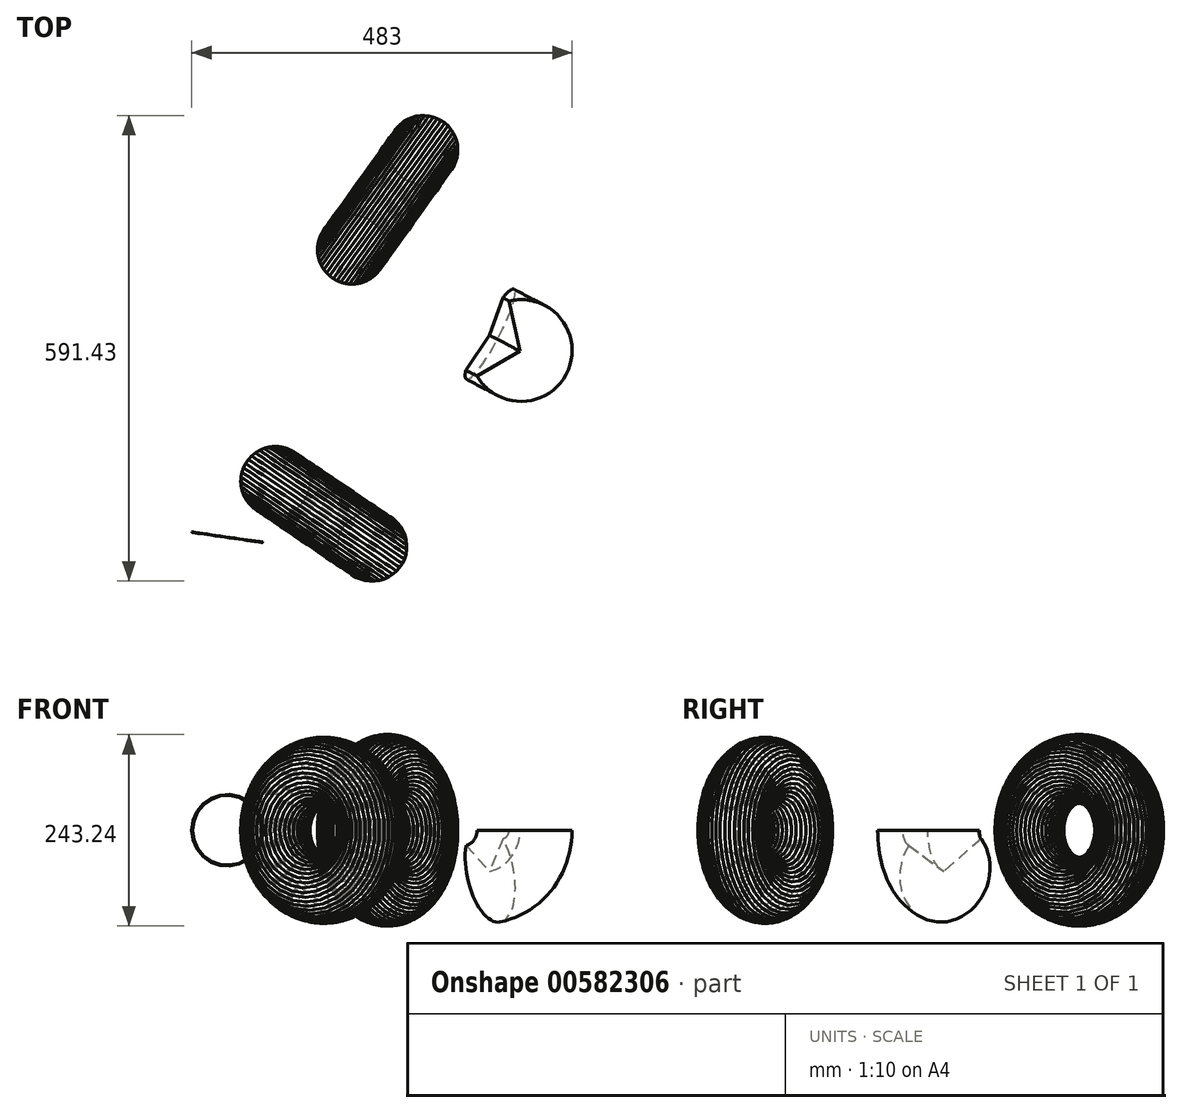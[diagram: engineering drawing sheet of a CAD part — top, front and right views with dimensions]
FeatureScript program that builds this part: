
annotation { "Feature Type Name" : "Feature", "Feature Type Description" : "" }
export const myFeature = defineFeature(function(context is Context, id is Id, definition is map)
    precondition{}
    {
        {
            var Q0;
            Q0=qCreatedBy(makeId("Top.planeOp"),FACE);
            var sketch = newSketch(context, id + "F0", { "sketchPlane" : qUnion([Q0])});
            skCircle(sketch, "E0.cCircle", {"center": v(-34.24, 57.95) * mm, "radius": 43.92 * mm, "construction": true});
            skLineSegment(sketch, "E0.0", {"start": v(1.92, 32.83) * mm, "end": v(-1.92, 28.04) * mm});
            skLineSegment(sketch, "E0.1", {"start": v(-1.92, 28.04) * mm, "end": v(-6.4, 23.84) * mm});
            skLineSegment(sketch, "E0.2", {"start": v(-6.4, 23.84) * mm, "end": v(-11.42, 20.3) * mm});
            skLineSegment(sketch, "E0.3", {"start": v(-11.42, 20.3) * mm, "end": v(-16.88, 17.48) * mm});
            skLineSegment(sketch, "E0.4", {"start": v(-16.88, 17.48) * mm, "end": v(-22.68, 15.46) * mm});
            skLineSegment(sketch, "E0.5", {"start": v(-22.68, 15.46) * mm, "end": v(-28.7, 14.27) * mm});
            skLineSegment(sketch, "E0.6", {"start": v(-28.7, 14.27) * mm, "end": v(-34.84, 13.92) * mm});
            skLineSegment(sketch, "E0.7", {"start": v(-34.84, 13.92) * mm, "end": v(-40.96, 14.44) * mm});
            skLineSegment(sketch, "E0.8", {"start": v(-40.96, 14.44) * mm, "end": v(-46.95, 15.8) * mm});
            skLineSegment(sketch, "E0.9", {"start": v(-46.95, 15.8) * mm, "end": v(-52.7, 17.97) * mm});
            skLineSegment(sketch, "E0.10", {"start": v(-52.7, 17.97) * mm, "end": v(-58.08, 20.93) * mm});
            skLineSegment(sketch, "E0.11", {"start": v(-58.08, 20.93) * mm, "end": v(-63, 24.6) * mm});
            skLineSegment(sketch, "E0.12", {"start": v(-63, 24.6) * mm, "end": v(-67.36, 28.94) * mm});
            skLineSegment(sketch, "E0.13", {"start": v(-67.36, 28.94) * mm, "end": v(-71.07, 33.83) * mm});
            skLineSegment(sketch, "E0.14", {"start": v(-71.07, 33.83) * mm, "end": v(-74.07, 39.19) * mm});
            skLineSegment(sketch, "E0.15", {"start": v(-74.07, 39.19) * mm, "end": v(-76.3, 44.92) * mm});
            skLineSegment(sketch, "E0.16", {"start": v(-76.3, 44.92) * mm, "end": v(-77.7, 50.9) * mm});
            skLineSegment(sketch, "E0.17", {"start": v(-77.7, 50.9) * mm, "end": v(-78.26, 57.01) * mm});
            skLineSegment(sketch, "E0.18", {"start": v(-78.26, 57.01) * mm, "end": v(-77.96, 63.15) * mm});
            skLineSegment(sketch, "E0.19", {"start": v(-77.96, 63.15) * mm, "end": v(-76.81, 69.18) * mm});
            skLineSegment(sketch, "E0.20", {"start": v(-76.81, 69.18) * mm, "end": v(-74.83, 75) * mm});
            skLineSegment(sketch, "E0.21", {"start": v(-74.83, 75) * mm, "end": v(-72.07, 80.48) * mm});
            skLineSegment(sketch, "E0.22", {"start": v(-72.07, 80.48) * mm, "end": v(-68.56, 85.53) * mm});
            skLineSegment(sketch, "E0.23", {"start": v(-68.56, 85.53) * mm, "end": v(-64.39, 90.04) * mm});
            skLineSegment(sketch, "E0.24", {"start": v(-64.39, 90.04) * mm, "end": v(-59.63, 93.92) * mm});
            skLineSegment(sketch, "E0.25", {"start": v(-59.63, 93.92) * mm, "end": v(-54.38, 97.1) * mm});
            skLineSegment(sketch, "E0.26", {"start": v(-54.38, 97.1) * mm, "end": v(-48.73, 99.52) * mm});
            skLineSegment(sketch, "E0.27", {"start": v(-48.73, 99.52) * mm, "end": v(-42.8, 101.14) * mm});
            skLineSegment(sketch, "E0.28", {"start": v(-42.8, 101.14) * mm, "end": v(-36.71, 101.9) * mm});
            skLineSegment(sketch, "E0.29", {"start": v(-36.71, 101.9) * mm, "end": v(-30.57, 101.83) * mm});
            skLineSegment(sketch, "E0.30", {"start": v(-30.57, 101.83) * mm, "end": v(-24.5, 100.89) * mm});
            skLineSegment(sketch, "E0.31", {"start": v(-24.5, 100.89) * mm, "end": v(-18.62, 99.11) * mm});
            skLineSegment(sketch, "E0.32", {"start": v(-18.62, 99.11) * mm, "end": v(-13.04, 96.54) * mm});
            skLineSegment(sketch, "E0.33", {"start": v(-13.04, 96.54) * mm, "end": v(-7.88, 93.21) * mm});
            skLineSegment(sketch, "E0.34", {"start": v(-7.88, 93.21) * mm, "end": v(-3.22, 89.2) * mm});
            skLineSegment(sketch, "E0.35", {"start": v(-3.22, 89.2) * mm, "end": v(0.82, 84.58) * mm});
            skLineSegment(sketch, "E0.36", {"start": v(0.82, 84.58) * mm, "end": v(4.19, 79.44) * mm});
            skLineSegment(sketch, "E0.37", {"start": v(4.19, 79.44) * mm, "end": v(6.8, 73.88) * mm});
            skLineSegment(sketch, "E0.38", {"start": v(6.8, 73.88) * mm, "end": v(8.62, 68.02) * mm});
            skLineSegment(sketch, "E0.39", {"start": v(8.62, 68.02) * mm, "end": v(9.6, 61.95) * mm});
            skLineSegment(sketch, "E0.40", {"start": v(9.6, 61.95) * mm, "end": v(9.74, 55.81) * mm});
            skLineSegment(sketch, "E0.41", {"start": v(9.74, 55.81) * mm, "end": v(9.01, 49.71) * mm});
            skLineSegment(sketch, "E0.42", {"start": v(9.01, 49.71) * mm, "end": v(7.45, 43.77) * mm});
            skLineSegment(sketch, "E0.43", {"start": v(7.45, 43.77) * mm, "end": v(5.07, 38.1) * mm});
            skLineSegment(sketch, "E0.44", {"start": v(5.07, 38.1) * mm, "end": v(1.92, 32.83) * mm});
            skPoint(sketch, "E0.0.midPoint", {"position": v(0, 30.44) * mm});
            skLineSegment(sketch, "E1", {"start": v(51.84, 53.07) * mm, "end": v(27.88, 17.57) * mm});
            skSolve(sketch);
        }
        {
            var Q0;
            Q0=makeQuery(id+"F0.imprint","IMPRINT",FACE,{"disambiguationData":[TD([[makeQuery(id+"F0.imprint","IMPRINT",EDGE,{"derivedFrom":sQuery(id+"F0.wireOp",EDGE,"E0.0")}),-1.0]])]});
            var Q1;
            Q1=sQuery(id+"F0.wireOp",EDGE,"E1");
            revolve(context, id + "F1", {"entities" : qUnion([Q0]), "axis" : qUnion([Q1]), "revolveType" : RevolveType.FULL});
        }
        {
            var Q0;
            Q0=qCreatedBy(makeId("Top.planeOp"),FACE);
            var sketch = newSketch(context, id + "F2", { "sketchPlane" : qUnion([Q0])});
            skArc(sketch, "E2", {"start": v(-86.8, -47.23) * mm, "mid": v(-6.4, -114.32) * mm, "end": v(-51.45, -19.79) * mm});
            skLineSegment(sketch, "E3", {"start": v(-105.95, -87.56) * mm, "end": v(-93.42, 0) * mm});
            skFitSpline(sketch, "E4", {"points": [v(-86.8, -47.23) * mm, v(-63.06, -53.03) * mm, v(-69.92, -34.56) * mm, v(-42.48, -47.23) * mm, v(-46.17, -31.93) * mm, v(-71.5, -29.81) * mm, v(-71.5, 0) * mm], "startDerivative": vector(209, -95.62) * mm, "endDerivative": vector(46.57, 214.63) * mm});
            skFitSpline(sketch, "E5", {"points": [v(-51.98, -11.35) * mm, v(-71.5, 0) * mm, v(-51.45, -19.79) * mm, v(-51.98, -11.35) * mm]});
            skSolve(sketch);
        }
        {
            var Q0;
            {var subQ0=sQuery(id+"F2.wireOp",EDGE,"E5");var subQ1=sQuery(id+"F2.wireOp",EDGE,"E2");var subQ2=makeQuery(id+"F2.imprint","INTERSECT",VERTEX,{"disambiguationData":[OD(0.0)],"derivedFrom":[subQ1,subQ0]});Q0=makeQuery(id+"F2.imprint","IMPRINT",FACE,{"disambiguationData":[TD([[makeQuery(id+"F2.imprint","IMPRINT",EDGE,{"disambiguationData":[TD([[subQ2,1.0]])],"derivedFrom":subQ1}),1.0]])]});}
            var Q1;
            Q1=sQuery(id+"F2.wireOp",EDGE,"E3");
            revolve(context, id + "F3", {"entities" : qUnion([Q0]), "axis" : qUnion([Q1]), "revolveType" : RevolveType.FULL, "oppositeDirection" : true});
        }
        {
            var Q0;
            Q0=qCreatedBy(makeId("Top.planeOp"),FACE);
            var sketch = newSketch(context, id + "F4", { "sketchPlane" : qUnion([Q0])});
            skArc(sketch, "E6", {"start": v(221.95, 191.5) * mm, "mid": v(337.4, 198.55) * mm, "end": v(262.6, 286.77) * mm});
            skLineSegment(sketch, "E7", {"start": v(262.6, 286.77) * mm, "end": v(276.39, 223.05) * mm});
            skLineSegment(sketch, "E8", {"start": v(221.95, 191.5) * mm, "end": v(277.91, 223.93) * mm});
            skPoint(sketch, "E9.orphan", {"position": v(277.91, 216.01) * mm});
            skLineSegment(sketch, "E10", {"start": v(238.8, 265.03) * mm, "end": v(211.56, 213.54) * mm});
            skSolve(sketch);
        }
        {
            var Q0;
            {var subQ0=sQuery(id+"F4.wireOp",EDGE,"E6");Q0=makeQuery(id+"F4.imprint","IMPRINT",FACE,{"disambiguationData":[TD([[makeQuery(id+"F4.imprint","IMPRINT",EDGE,{"derivedFrom":subQ0}),1.0]])]});}
            var Q1;
            Q1=sQuery(id+"F4.wireOp",EDGE,"E10");
            revolve(context, id + "F5", {"entities" : qUnion([Q0]), "axis" : qUnion([Q1]), "revolveType" : RevolveType.ONE_DIRECTION, "oppositeDirection" : true, "angle" : 80 * degree});
        }
        {
            var Q0;
            Q0=qCreatedBy(makeId("Top.planeOp"),FACE);
            var sketch = newSketch(context, id + "F6", { "sketchPlane" : qUnion([Q0])});
            skCircle(sketch, "E11.cCircle", {"center": v(62.94, 352.07) * mm, "radius": 43.7 * mm, "construction": true});
            skLineSegment(sketch, "E11.0", {"start": v(81.95, 391.42) * mm, "end": v(86.73, 388.73) * mm});
            skLineSegment(sketch, "E11.1", {"start": v(86.73, 388.73) * mm, "end": v(91.14, 385.46) * mm});
            skLineSegment(sketch, "E11.2", {"start": v(91.14, 385.46) * mm, "end": v(95.1, 381.66) * mm});
            skLineSegment(sketch, "E11.3", {"start": v(95.1, 381.66) * mm, "end": v(98.55, 377.4) * mm});
            skLineSegment(sketch, "E11.4", {"start": v(98.55, 377.4) * mm, "end": v(101.45, 372.73) * mm});
            skLineSegment(sketch, "E11.5", {"start": v(101.45, 372.73) * mm, "end": v(103.73, 367.74) * mm});
            skLineSegment(sketch, "E11.6", {"start": v(103.73, 367.74) * mm, "end": v(105.38, 362.5) * mm});
            skLineSegment(sketch, "E11.7", {"start": v(105.38, 362.5) * mm, "end": v(106.35, 357.1) * mm});
            skLineSegment(sketch, "E11.8", {"start": v(106.35, 357.1) * mm, "end": v(106.64, 351.63) * mm});
            skLineSegment(sketch, "E11.9", {"start": v(106.64, 351.63) * mm, "end": v(106.24, 346.15) * mm});
            skLineSegment(sketch, "E11.10", {"start": v(106.24, 346.15) * mm, "end": v(105.16, 340.77) * mm});
            skLineSegment(sketch, "E11.11", {"start": v(105.16, 340.77) * mm, "end": v(103.41, 335.57) * mm});
            skLineSegment(sketch, "E11.12", {"start": v(103.41, 335.57) * mm, "end": v(101.02, 330.63) * mm});
            skLineSegment(sketch, "E11.13", {"start": v(101.02, 330.63) * mm, "end": v(98.04, 326.03) * mm});
            skLineSegment(sketch, "E11.14", {"start": v(98.04, 326.03) * mm, "end": v(94.5, 321.83) * mm});
            skLineSegment(sketch, "E11.15", {"start": v(94.5, 321.83) * mm, "end": v(90.46, 318.12) * mm});
            skLineSegment(sketch, "E11.16", {"start": v(90.46, 318.12) * mm, "end": v(85.99, 314.93) * mm});
            skLineSegment(sketch, "E11.17", {"start": v(85.99, 314.93) * mm, "end": v(81.15, 312.34) * mm});
            skLineSegment(sketch, "E11.18", {"start": v(81.15, 312.34) * mm, "end": v(76.03, 310.37) * mm});
            skLineSegment(sketch, "E11.19", {"start": v(76.03, 310.37) * mm, "end": v(70.7, 309.06) * mm});
            skLineSegment(sketch, "E11.20", {"start": v(70.7, 309.06) * mm, "end": v(65.25, 308.43) * mm});
            skLineSegment(sketch, "E11.21", {"start": v(65.25, 308.43) * mm, "end": v(59.76, 308.48) * mm});
            skLineSegment(sketch, "E11.22", {"start": v(59.76, 308.48) * mm, "end": v(54.32, 309.22) * mm});
            skLineSegment(sketch, "E11.23", {"start": v(54.32, 309.22) * mm, "end": v(49.02, 310.64) * mm});
            skLineSegment(sketch, "E11.24", {"start": v(49.02, 310.64) * mm, "end": v(43.94, 312.71) * mm});
            skLineSegment(sketch, "E11.25", {"start": v(43.94, 312.71) * mm, "end": v(39.16, 315.4) * mm});
            skLineSegment(sketch, "E11.26", {"start": v(39.16, 315.4) * mm, "end": v(34.75, 318.68) * mm});
            skLineSegment(sketch, "E11.27", {"start": v(34.75, 318.68) * mm, "end": v(30.79, 322.47) * mm});
            skLineSegment(sketch, "E11.28", {"start": v(30.79, 322.47) * mm, "end": v(27.33, 326.74) * mm});
            skLineSegment(sketch, "E11.29", {"start": v(27.33, 326.74) * mm, "end": v(24.44, 331.4) * mm});
            skLineSegment(sketch, "E11.30", {"start": v(24.44, 331.4) * mm, "end": v(22.15, 336.39) * mm});
            skLineSegment(sketch, "E11.31", {"start": v(22.15, 336.39) * mm, "end": v(20.5, 341.62) * mm});
            skLineSegment(sketch, "E11.32", {"start": v(20.5, 341.62) * mm, "end": v(19.53, 347.02) * mm});
            skLineSegment(sketch, "E11.33", {"start": v(19.53, 347.02) * mm, "end": v(19.24, 352.5) * mm});
            skLineSegment(sketch, "E11.34", {"start": v(19.24, 352.5) * mm, "end": v(19.64, 357.98) * mm});
            skLineSegment(sketch, "E11.35", {"start": v(19.64, 357.98) * mm, "end": v(20.73, 363.36) * mm});
            skLineSegment(sketch, "E11.36", {"start": v(20.73, 363.36) * mm, "end": v(22.47, 368.56) * mm});
            skLineSegment(sketch, "E11.37", {"start": v(22.47, 368.56) * mm, "end": v(24.86, 373.5) * mm});
            skLineSegment(sketch, "E11.38", {"start": v(24.86, 373.5) * mm, "end": v(27.85, 378.1) * mm});
            skLineSegment(sketch, "E11.39", {"start": v(27.85, 378.1) * mm, "end": v(31.39, 382.3) * mm});
            skLineSegment(sketch, "E11.40", {"start": v(31.39, 382.3) * mm, "end": v(35.43, 386.02) * mm});
            skLineSegment(sketch, "E11.41", {"start": v(35.43, 386.02) * mm, "end": v(39.9, 389.2) * mm});
            skLineSegment(sketch, "E11.42", {"start": v(39.9, 389.2) * mm, "end": v(44.73, 391.8) * mm});
            skLineSegment(sketch, "E11.43", {"start": v(44.73, 391.8) * mm, "end": v(49.86, 393.76) * mm});
            skLineSegment(sketch, "E11.44", {"start": v(49.86, 393.76) * mm, "end": v(55.19, 395.07) * mm});
            skLineSegment(sketch, "E11.45", {"start": v(55.19, 395.07) * mm, "end": v(60.64, 395.7) * mm});
            skLineSegment(sketch, "E11.46", {"start": v(60.64, 395.7) * mm, "end": v(66.12, 395.65) * mm});
            skLineSegment(sketch, "E11.47", {"start": v(66.12, 395.65) * mm, "end": v(71.56, 394.9) * mm});
            skLineSegment(sketch, "E11.48", {"start": v(71.56, 394.9) * mm, "end": v(76.86, 393.5) * mm});
            skLineSegment(sketch, "E11.49", {"start": v(76.86, 393.5) * mm, "end": v(81.95, 391.42) * mm});
            skLineSegment(sketch, "E12", {"start": v(87.1, 430.66) * mm, "end": v(140.47, 392.45) * mm});
            skSolve(sketch);
        }
        {
            var Q0;
            Q0=makeQuery(id+"F6.imprint","IMPRINT",FACE,{"disambiguationData":[TD([[makeQuery(id+"F6.imprint","IMPRINT",EDGE,{"derivedFrom":sQuery(id+"F6.wireOp",EDGE,"E11.0")}),-1.0]])]});
            var Q1;
            Q1=sQuery(id+"F6.wireOp",EDGE,"E12");
            revolve(context, id + "F7", {"entities" : qUnion([Q0]), "axis" : qUnion([Q1]), "revolveType" : RevolveType.FULL});
        }
    });
